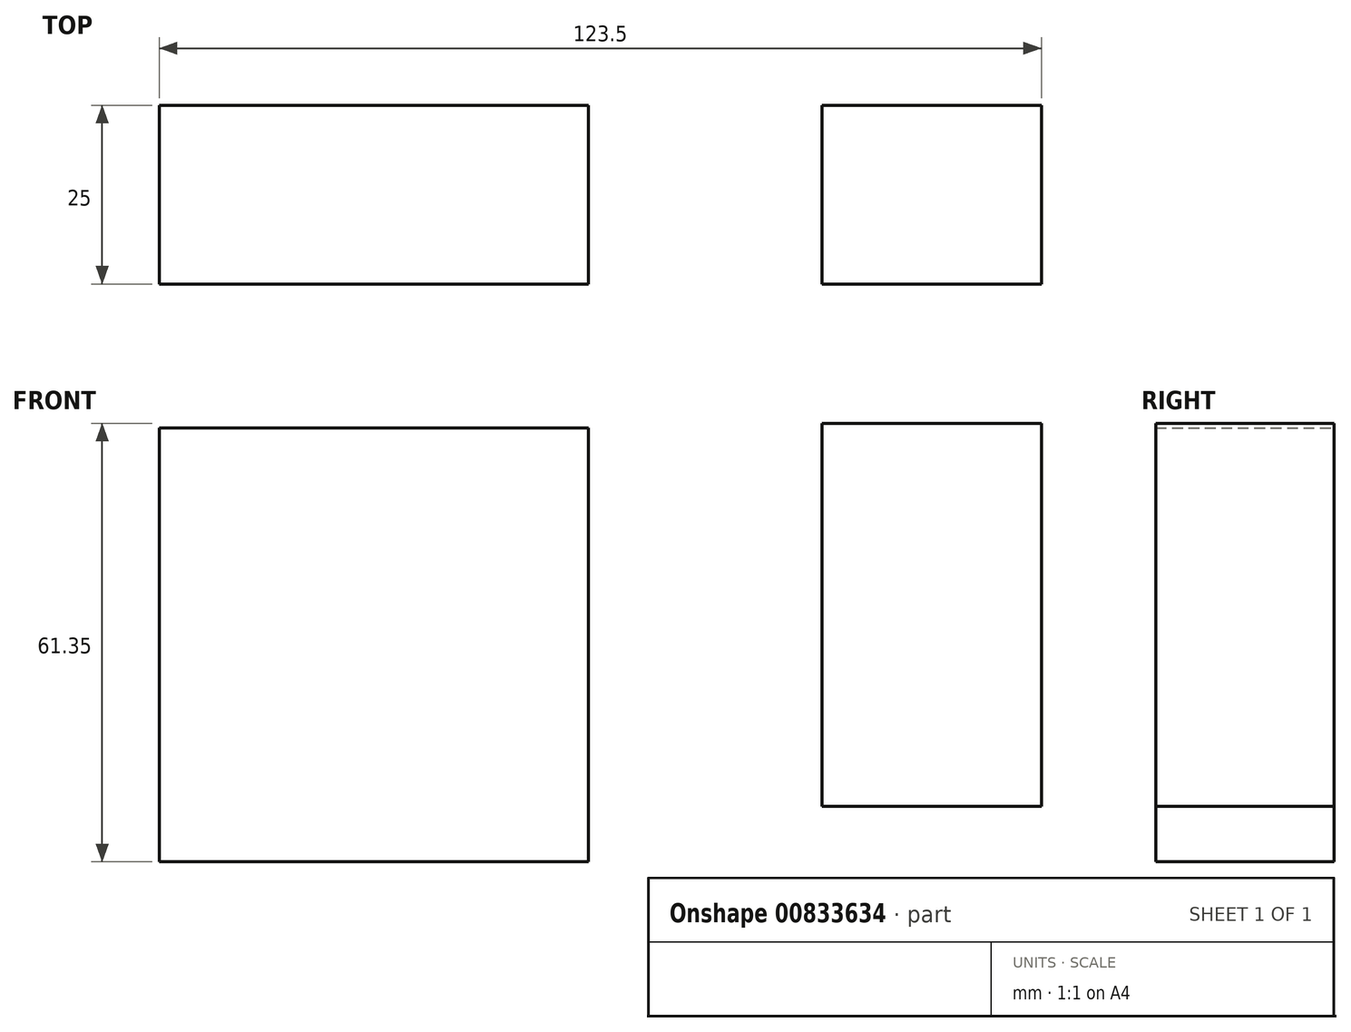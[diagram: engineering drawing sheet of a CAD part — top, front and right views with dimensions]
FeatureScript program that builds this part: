
annotation { "Feature Type Name" : "Feature", "Feature Type Description" : "" }
export const myFeature = defineFeature(function(context is Context, id is Id, definition is map)
    precondition{}
    {
        {
            var Q0;
            Q0=qCreatedBy(makeId("Front.planeOp"),FACE);
            var sketch = newSketch(context, id + "F0", { "sketchPlane" : qUnion([Q0])});
            skLineSegment(sketch, "E0.bottom", {"start": v(-142.7, 23.73) * mm, "end": v(-82.61, 23.73) * mm});
            skLineSegment(sketch, "E0.top", {"start": v(-142.7, 84.47) * mm, "end": v(-82.61, 84.47) * mm});
            skLineSegment(sketch, "E0.left", {"start": v(-142.7, 23.73) * mm, "end": v(-142.7, 84.47) * mm});
            skLineSegment(sketch, "E0.right", {"start": v(-82.61, 23.73) * mm, "end": v(-82.61, 84.47) * mm});
            skPoint(sketch, "E0.middle", {"position": v(-112.65, 54.1) * mm});
            skLineSegment(sketch, "E1.bottom", {"start": v(-49.9, 31.5) * mm, "end": v(-19.2, 31.5) * mm});
            skLineSegment(sketch, "E1.top", {"start": v(-49.9, 85.08) * mm, "end": v(-19.2, 85.08) * mm});
            skLineSegment(sketch, "E1.left", {"start": v(-49.9, 31.5) * mm, "end": v(-49.9, 85.08) * mm});
            skLineSegment(sketch, "E1.right", {"start": v(-19.2, 31.5) * mm, "end": v(-19.2, 85.08) * mm});
            skPoint(sketch, "E1.middle", {"position": v(-34.55, 58.29) * mm});
            skSolve(sketch);
        }
        {
            var Q0;
            Q0=makeQuery(id+"F0.imprint","IMPRINT",FACE,{"disambiguationData":[TD([[makeQuery(id+"F0.imprint","IMPRINT",EDGE,{"derivedFrom":sQuery(id+"F0.wireOp",EDGE,"E0.bottom")}),1.0]])]});
            var Q1;
            Q1=makeQuery(id+"F0.imprint","IMPRINT",FACE,{"disambiguationData":[TD([[makeQuery(id+"F0.imprint","IMPRINT",EDGE,{"derivedFrom":sQuery(id+"F0.wireOp",EDGE,"E1.bottom")}),1.0]])]});
            extrude(context, id + "F1", {"entities" : qUnion([Q0, Q1]), "depth" : 25 * mm, "offsetDistance" : 25 * mm});
        }
    });
